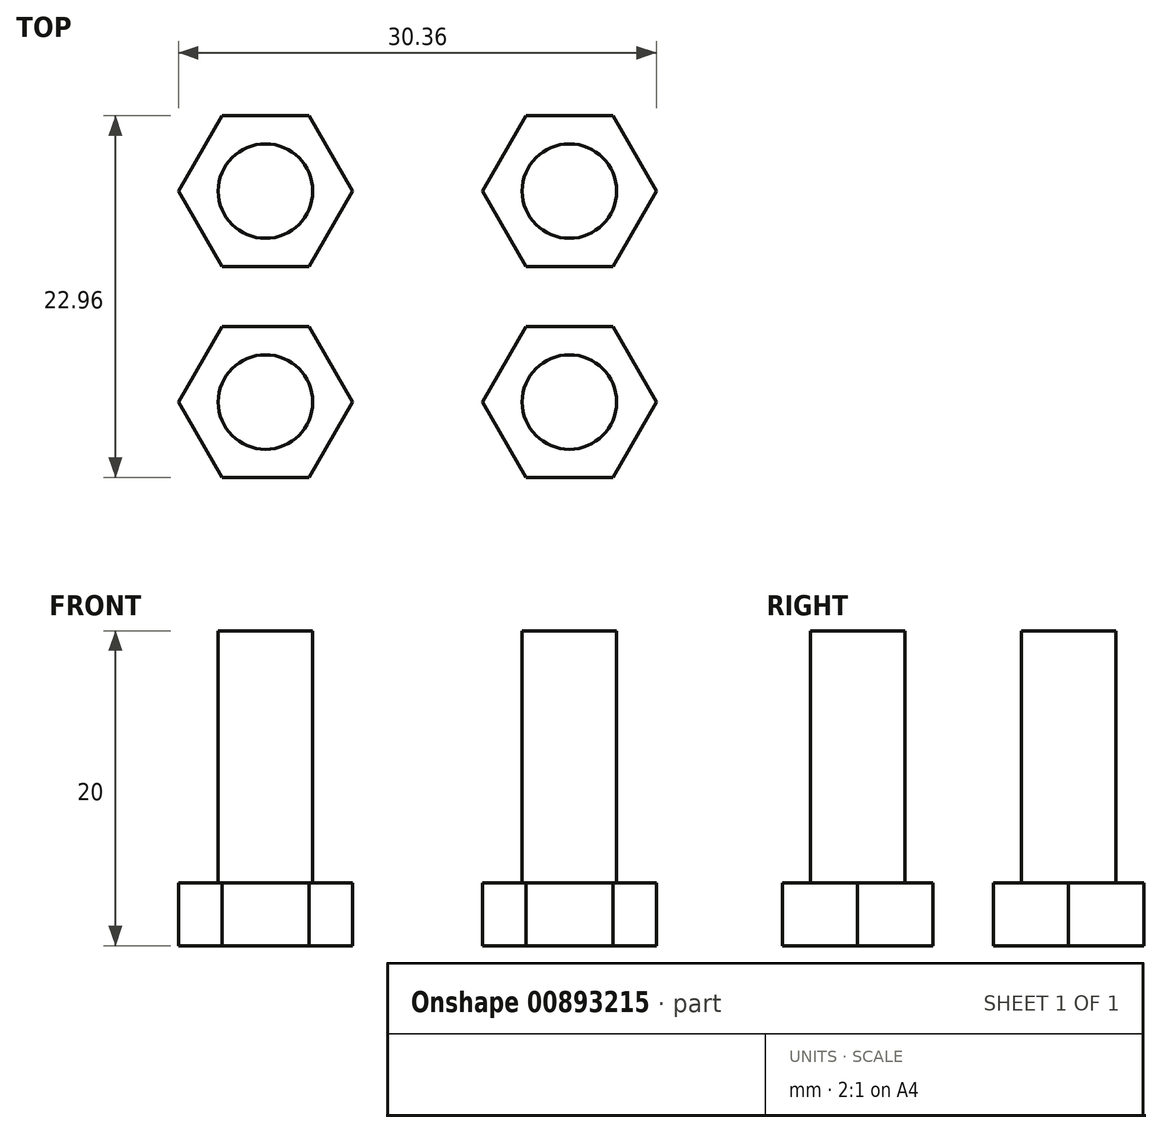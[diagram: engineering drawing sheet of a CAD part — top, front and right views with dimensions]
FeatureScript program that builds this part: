
annotation { "Feature Type Name" : "Feature", "Feature Type Description" : "" }
export const myFeature = defineFeature(function(context is Context, id is Id, definition is map)
    precondition{}
    {
        {
            var Q0;
            Q0=qCreatedBy(makeId("Top.planeOp"),FACE);
            var sketch = newSketch(context, id + "F0", { "sketchPlane" : qUnion([Q0])});
            skCircle(sketch, "E0.cCircle", {"center": v(-9.65, 0) * mm, "radius": 4.78 * mm, "construction": true});
            skLineSegment(sketch, "E0.0", {"start": v(-12.41, 4.78) * mm, "end": v(-6.89, 4.78) * mm});
            skLineSegment(sketch, "E0.1", {"start": v(-6.89, 4.78) * mm, "end": v(-4.13, 0) * mm});
            skLineSegment(sketch, "E0.2", {"start": v(-4.13, 0) * mm, "end": v(-6.89, -4.78) * mm});
            skLineSegment(sketch, "E0.3", {"start": v(-6.89, -4.78) * mm, "end": v(-12.41, -4.78) * mm});
            skLineSegment(sketch, "E0.4", {"start": v(-12.41, -4.78) * mm, "end": v(-15.18, 0) * mm});
            skLineSegment(sketch, "E0.5", {"start": v(-15.18, 0) * mm, "end": v(-12.41, 4.78) * mm});
            skPoint(sketch, "E0.0.midPoint", {"position": v(-9.65, 4.78) * mm});
            skSolve(sketch);
        }
        {
            var Q0;
            Q0=makeQuery(id+"F0.imprint","IMPRINT",FACE,{"disambiguationData":[TD([[makeQuery(id+"F0.imprint","IMPRINT",EDGE,{"derivedFrom":sQuery(id+"F0.wireOp",EDGE,"E0.0")}),-1.0]])]});
            extrude(context, id + "F1", {"entities" : qUnion([Q0]), "depth" : 4 * mm, "offsetDistance" : 25 * mm});
        }
        {
            var Q0;
            Q0=makeQuery(id+"F1.opExtrude","CAP_FACE",FACE,{"disambiguationData":[OSD([sQuery(id+"F0.wireOp",EDGE,"E0.0"),sQuery(id+"F0.wireOp",EDGE,"E0.1"),sQuery(id+"F0.wireOp",EDGE,"E0.2"),sQuery(id+"F0.wireOp",EDGE,"E0.3"),sQuery(id+"F0.wireOp",EDGE,"E0.4"),sQuery(id+"F0.wireOp",EDGE,"E0.5")])],"isStart":false});
            var sketch = newSketch(context, id + "F2", { "sketchPlane" : qUnion([Q0])});
            skCircle(sketch, "E1", {"center": v(-9.65, 0) * mm, "radius": 3 * mm});
            skPoint(sketch, "E1.centerSnap0", {"position": v(-9.65, 4.78) * mm});
            skSolve(sketch);
        }
        {
            var Q0;
            Q0=makeQuery(id+"F2.imprint","IMPRINT",FACE,{"disambiguationData":[TD([[makeQuery(id+"F2.imprint","IMPRINT",EDGE,{"derivedFrom":sQuery(id+"F2.wireOp",EDGE,"E1")}),1.0]])]});
            extrude(context, id + "F3", {"entities" : qUnion([Q0]), "operationType" : NewBodyOperationType.ADD, "depth" : 16 * mm, "offsetDistance" : 25 * mm});
        }
        {
            var Q0;
            Q0=makeQuery(id+"F1.opExtrude","SWEPT_BODY",BODY,{"disambiguationData":[OSD([sQuery(id+"F0.wireOp",EDGE,"E0.0"),sQuery(id+"F0.wireOp",EDGE,"E0.1"),sQuery(id+"F0.wireOp",EDGE,"E0.2"),sQuery(id+"F0.wireOp",EDGE,"E0.3"),sQuery(id+"F0.wireOp",EDGE,"E0.4"),sQuery(id+"F0.wireOp",EDGE,"E0.5")])]});
            var Q1;
            Q1=qCreatedBy(makeId("Right.planeOp"),FACE);
            mirror(context, id + "F4", {"entities" : qUnion([Q0]), "mirrorPlane" : qUnion([Q1])});
        }
        {
            var Q0;
            Q0=qCreatedBy(makeId("Front.planeOp"),FACE);
            cPlane(context, id + "F5", {"entities" : qUnion([Q0]), "cplaneType" : CPlaneType.OFFSET, "offset" : 6.7 * mm, "width" : 150 * mm, "height" : 150 * mm});
        }
        {
            var Q0;
            Q0=makeQuery(id+"F1.opExtrude","SWEPT_BODY",BODY,{"disambiguationData":[OSD([sQuery(id+"F0.wireOp",EDGE,"E0.0"),sQuery(id+"F0.wireOp",EDGE,"E0.1"),sQuery(id+"F0.wireOp",EDGE,"E0.2"),sQuery(id+"F0.wireOp",EDGE,"E0.3"),sQuery(id+"F0.wireOp",EDGE,"E0.4"),sQuery(id+"F0.wireOp",EDGE,"E0.5")])]});
            var Q1;
            Q1=makeQuery(id+"F4.opPattern","COPY",BODY,{"derivedFrom":makeQuery(id+"F1.opExtrude","SWEPT_BODY",BODY,{"disambiguationData":[OSD([sQuery(id+"F0.wireOp",EDGE,"E0.0"),sQuery(id+"F0.wireOp",EDGE,"E0.1"),sQuery(id+"F0.wireOp",EDGE,"E0.2"),sQuery(id+"F0.wireOp",EDGE,"E0.3"),sQuery(id+"F0.wireOp",EDGE,"E0.4"),sQuery(id+"F0.wireOp",EDGE,"E0.5")])]}),"instanceName":"1"});
            var Q2;
            Q2=qCreatedBy(id+"F5.planeOp",FACE);
            mirror(context, id + "F6", {"entities" : qUnion([Q0, Q1]), "mirrorPlane" : qUnion([Q2])});
        }
    });
